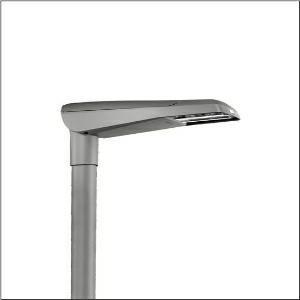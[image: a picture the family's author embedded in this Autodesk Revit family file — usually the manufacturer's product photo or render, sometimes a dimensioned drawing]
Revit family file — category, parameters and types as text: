
# Revit family: streetlight_sl_11_iq_micro___st1_2a_5xc1a31f08ce_a0bf
name_source: partatom
category: Lighting Fixtures
units: mm (PartAtom-declared; Revit-internal decimal feet)

## family parameters
Cut with Voids When Loaded = No
Host = Face
Light Source = No
Part Type = Normal
Room Calculation Point = No
Round Connector Dimension = Use Diameter
Shared = No

## types (1)
- --- (1 x LED, 1620 lm, 12.6 W, 3000K)
    Apparent Load = 13 VA
    CIE Flux Codes = 33 71 96 100 100
    Color Rendering = 80
    Color Temperature = 3000K
    Default Elevation = 1800 mm
    Description = Streetlight SL 11 iQ micro, mast luminaire, primary light control with 3 zone facetted reflector, of plastic, silver coated, highly specular, primary optical cover: cover, of PMMA, transparent, light distribution: ST1.2a, light emission: direct distribution, primary light characteristic: asymmetric, installation type: post-top, side-entry, lamps: LED, High Power LED, rated values: 1.620lm | 12,6W | 128,6lm/W (begin service life); end service life: 1.620lm | 12,9W; at 50% lumin. flux: 810lm | 6,8W | 119,1lm/W, colour temperature: 3000K, colour rendering: CRI > 80, light colour: 830, light setting 1 begin service life: 100% | 1.620lm | 12,6W | 128,6lm/W | 3.000K, light setting 1 end service life: 12,9W, further light settings possible, control: Street-Remote, optimised constant luminous flux control (CLO 2.0), Desk-Remote (wireless, voltage-free reading and setting of iQ features in the workshop via application-optimized NFC function/RFID function), Light-Fading, Smart-Wire, Night-Set, Lumen-Switch, Temp-Guard, Auto-Match, with cable H07RN-F 3x 1.5mm², mains connection: 230..240V, AC, 50/60Hz, connection cable pre-assembled, cable length: 5,5m, luminaire housing, of diecast aluminium, powder-coated, SITECO metallic grey (DB 702S), please order mast flange separately, inclination adjustable without tools: 0°, 5°, 10°, 15° (post-top) | 0°, -5°, -10°, -15° (side-entry), sealing non-destructively replaceable, multi-level sealing system, length: 600mm, width: 174mm, height: 116mm, mast flange for spigot size: 42mm (side-entry): 5XC10008XM4, 60/48mm (side-entry/post-top): 5XC10108XM2, 76/60mm (side-entry/post-top): 5XC10108XM1, equipment: standard, protection rating (complete): IP66, insulation class (complete): insulation class II (safety insulation), certification: CE, ENEC, ENEC+, VDE, impact resistance: IK10, permissible operating ambient temperature for outdoor applications: -25..+50°C, standard-compliant lighting for roads and squares, Environmental Product Declaration (EPD) tested and certified by an independent institute, packaging unit: 1 piece

Light Distribution: ST1.2a
    Height = 116 mm
    Lamp = 1 x LED
    Lamp Light Flux = 1620 lm
    Lamp Power = 12.6 W
    Lamp count = 1
    Length = 600 mm
    Luminous efficacy = 129 lm/W
    Manufacturer = Siteco
    ModVariant = No
    Model = 5XC1A31F08CE
    Number of Poles = 1
    OnlyDefault = Yes
    Power Factor = 1
    Product Name = Streetlight SL 11 iQ micro | ST1.2a
    Product group = mast luminaire | pylon top
    ProductGroupID = 6100
    Protection Class = Protection class II
    Protection Degree = IP 66
    RLX_Detail_Level = 1
    RLX_Emergency_Light_Flux = 0 lm
    RLX_Emergency_Type = 0
    RLX_Emergency_Type_DB = No
    RlxData = <blob elided: 26541 chars, md5=174bc542>
    Socket = socket
    Standby Power = 0 W
    System Light Flux = 1620 lm
    System Power = 13 W
    Type Comments = factory setting: luminous flux: 100 % | dim-lin: 254 | 229 mA
    Type Image = l_1006566.jpg
    URL = http://relux.com
    VarID = @adj_019073
    Voltage = 0 V
    Weight = 0.00 kg
    Width = 174 mm

## geometry (parser evidence)
native form markers: Blend x4, Sweep x13
no freeform markers — native parametric forms only
